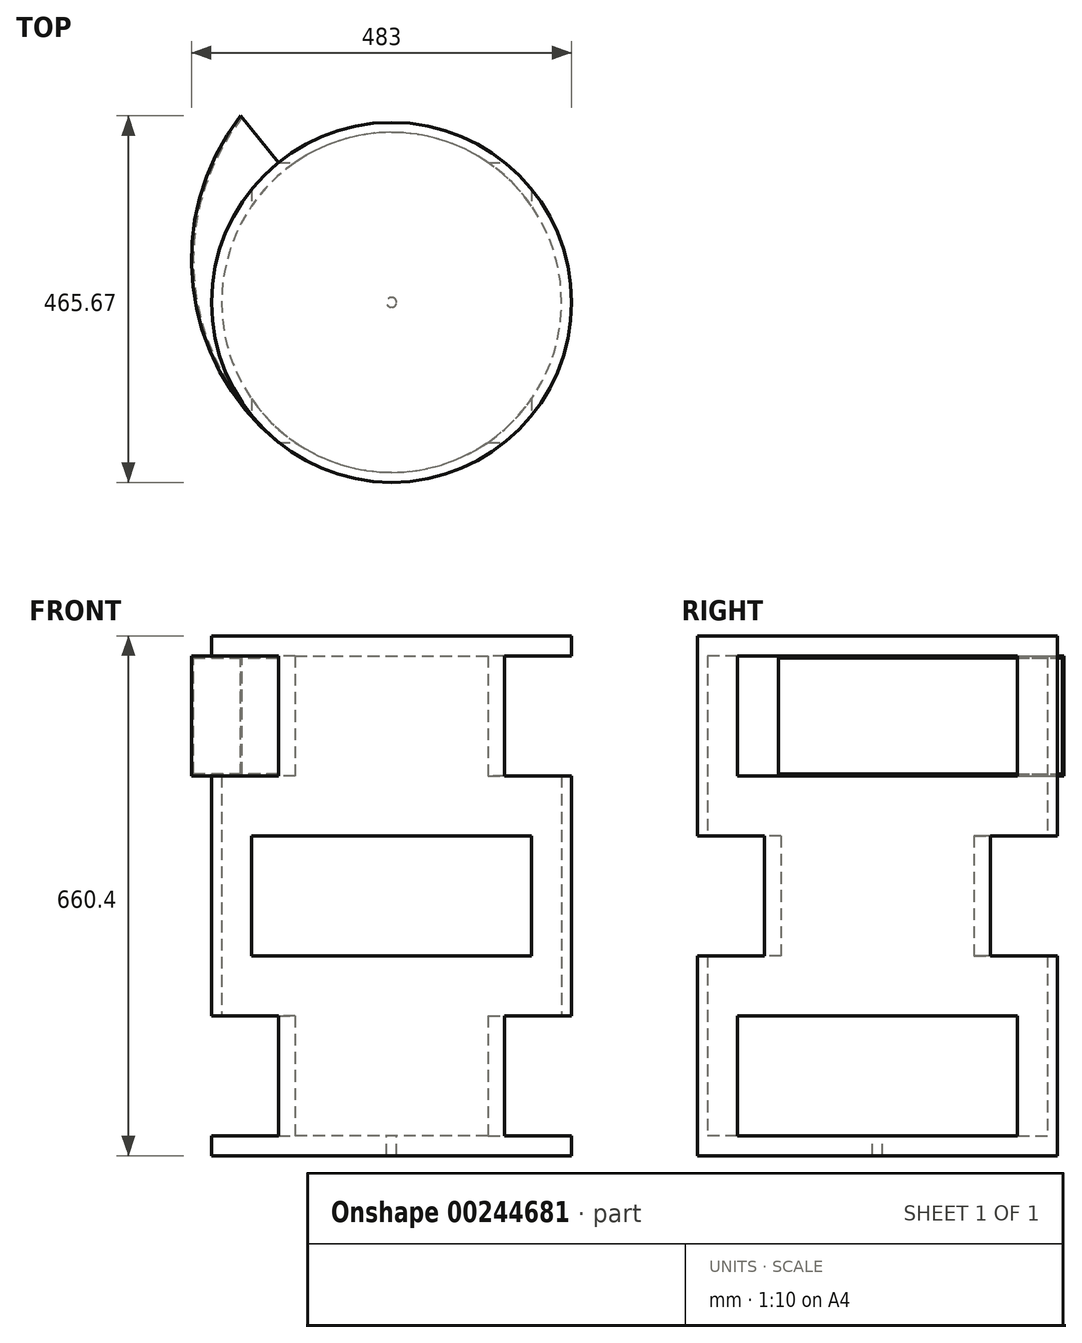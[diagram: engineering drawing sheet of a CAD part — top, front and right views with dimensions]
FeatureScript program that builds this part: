
annotation { "Feature Type Name" : "Feature", "Feature Type Description" : "" }
export const myFeature = defineFeature(function(context is Context, id is Id, definition is map)
    precondition{}
    {
        {
            var Q0;
            Q0=qCreatedBy(makeId("Top.planeOp"),FACE);
            var sketch = newSketch(context, id + "F0", { "sketchPlane" : qUnion([Q0])});
            skCircle(sketch, "E0", {"center": v(0, 0) * mm, "radius": 228.6 * mm});
            skSolve(sketch);
        }
        {
            var Q0;
            Q0=makeQuery(id+"F0.imprint","IMPRINT",FACE,{"disambiguationData":[TD([[makeQuery(id+"F0.imprint","IMPRINT",EDGE,{"derivedFrom":sQuery(id+"F0.wireOp",EDGE,"E0")}),1.0]])]});
            extrude(context, id + "F1", {"entities" : qUnion([Q0]), "depth" : 330.2 * mm, "hasSecondDirection" : true, "secondDirectionOppositeDirection" : true, "secondDirectionDepth" : 330.2 * mm});
        }
        {
            var Q0;
            Q0=makeQuery(id+"F1.opExtrude","CAP_FACE",FACE,{"disambiguationData":[OSD([sQuery(id+"F0.wireOp",EDGE,"E0")])],"isStart":false});
            var Q1;
            Q1=makeQuery(id+"F1.opExtrude","CAP_FACE",FACE,{"disambiguationData":[OSD([sQuery(id+"F0.wireOp",EDGE,"E0")])],"isStart":true});
            shell(context, id + "F2", {"entities" : qUnion([Q0, Q1]), "thickness" : 12.7 * mm});
        }
        {
            var Q0;
            Q0=qCreatedBy(makeId("Front.planeOp"),FACE);
            cPlane(context, id + "F3", {"entities" : qUnion([Q0]), "cplaneType" : CPlaneType.OFFSET, "offset" : 228.6 * mm, "width" : 152.4 * mm, "height" : 152.4 * mm});
        }
        {
            var Q0;
            Q0=qCreatedBy(makeId("Right.planeOp"),FACE);
            cPlane(context, id + "F4", {"entities" : qUnion([Q0]), "cplaneType" : CPlaneType.OFFSET, "offset" : 228.6 * mm, "oppositeDirection" : true, "width" : 152.4 * mm, "height" : 152.4 * mm});
        }
        {
            var Q0;
            Q0=qCreatedBy(makeId("Right.planeOp"),FACE);
            cPlane(context, id + "F5", {"entities" : qUnion([Q0]), "cplaneType" : CPlaneType.OFFSET, "offset" : 228.6 * mm, "width" : 152.4 * mm, "height" : 152.4 * mm});
        }
        {
            var Q0;
            Q0=qCreatedBy(id+"F5.planeOp",FACE);
            var sketch = newSketch(context, id + "F6", { "sketchPlane" : qUnion([Q0])});
            skLineSegment(sketch, "E1", {"start": v(0, 0) * mm, "end": v(0, -304.8) * mm, "construction": true});
            skLineSegment(sketch, "E2", {"start": v(0, 0) * mm, "end": v(0, 330.2) * mm, "construction": true});
            skPoint(sketch, "E3", {"position": v(0, -152.4) * mm});
            skLineSegment(sketch, "E4", {"start": v(0, 0) * mm, "end": v(186.3, 0) * mm, "construction": true});
            skPoint(sketch, "E5.MirrorP", {"position": v(0, 152.4) * mm});
            skLineSegment(sketch, "E6.bottom", {"start": v(177.8, -152.4) * mm, "end": v(-177.8, -152.4) * mm});
            skLineSegment(sketch, "E6.top", {"start": v(177.8, -304.8) * mm, "end": v(-177.8, -304.8) * mm});
            skLineSegment(sketch, "E6.left", {"start": v(177.8, -152.4) * mm, "end": v(177.8, -304.8) * mm});
            skLineSegment(sketch, "E6.right", {"start": v(-177.8, -152.4) * mm, "end": v(-177.8, -304.8) * mm});
            skSolve(sketch);
        }
        {
            var Q0;
            Q0=makeQuery(id+"F6.imprint","IMPRINT",FACE,{"disambiguationData":[TD([[makeQuery(id+"F6.imprint","IMPRINT",EDGE,{"derivedFrom":sQuery(id+"F6.wireOp",EDGE,"E6.bottom")}),1.0]])]});
            extrude(context, id + "F7", {"entities" : qUnion([Q0]), "operationType" : NewBodyOperationType.REMOVE, "oppositeDirection" : true, "depth" : 457.2 * mm});
        }
        {
            var Q0;
            Q0=qCreatedBy(id+"F4.planeOp",FACE);
            var sketch = newSketch(context, id + "F8", { "sketchPlane" : qUnion([Q0])});
            skLineSegment(sketch, "E7", {"start": v(0, 0) * mm, "end": v(0, 304.8) * mm, "construction": true});
            skLineSegment(sketch, "E8", {"start": v(0, 0) * mm, "end": v(-120.1, 0) * mm, "construction": true});
            skPoint(sketch, "E9", {"position": v(0, 152.4) * mm});
            skLineSegment(sketch, "E10.bottom", {"start": v(-177.8, 304.8) * mm, "end": v(177.8, 304.8) * mm});
            skLineSegment(sketch, "E10.top", {"start": v(-177.8, 152.4) * mm, "end": v(177.8, 152.4) * mm});
            skLineSegment(sketch, "E10.left", {"start": v(-177.8, 304.8) * mm, "end": v(-177.8, 152.4) * mm});
            skLineSegment(sketch, "E10.right", {"start": v(177.8, 304.8) * mm, "end": v(177.8, 152.4) * mm});
            skSolve(sketch);
        }
        {
            var Q0;
            Q0=makeQuery(id+"F8.imprint","IMPRINT",FACE,{"disambiguationData":[TD([[makeQuery(id+"F8.imprint","IMPRINT",EDGE,{"derivedFrom":sQuery(id+"F8.wireOp",EDGE,"E10.bottom")}),-1.0]])]});
            extrude(context, id + "F9", {"entities" : qUnion([Q0]), "operationType" : NewBodyOperationType.REMOVE, "depth" : 457.2 * mm});
        }
        {
            var Q0;
            Q0=qCreatedBy(id+"F3.planeOp",FACE);
            var sketch = newSketch(context, id + "F10", { "sketchPlane" : qUnion([Q0])});
            skLineSegment(sketch, "E11", {"start": v(0, 0) * mm, "end": v(0, -330.2) * mm, "construction": true});
            skLineSegment(sketch, "E12.bottom", {"start": v(177.8, -76.2) * mm, "end": v(-177.8, -76.2) * mm});
            skLineSegment(sketch, "E12.top", {"start": v(177.8, 76.2) * mm, "end": v(-177.8, 76.2) * mm});
            skLineSegment(sketch, "E12.left", {"start": v(177.8, -76.2) * mm, "end": v(177.8, 76.2) * mm});
            skLineSegment(sketch, "E12.right", {"start": v(-177.8, -76.2) * mm, "end": v(-177.8, 76.2) * mm});
            skPoint(sketch, "E13", {"position": v(0, -76.2) * mm});
            skSolve(sketch);
        }
        {
            var Q0;
            Q0=makeQuery(id+"F10.imprint","IMPRINT",FACE,{"disambiguationData":[TD([[makeQuery(id+"F10.imprint","IMPRINT",EDGE,{"derivedFrom":sQuery(id+"F10.wireOp",EDGE,"E12.bottom")}),-1.0]])]});
            extrude(context, id + "F11", {"entities" : qUnion([Q0]), "operationType" : NewBodyOperationType.REMOVE, "oppositeDirection" : true, "depth" : 457.2 * mm});
        }
        {
            var Q0;
            Q0=makeQuery(id+"F9.boolean.opBoolean","COPY",FACE,{"disambiguationData":[OD(0.0)],"derivedFrom":makeQuery(id+"F9.opExtrude","SWEPT_FACE",FACE,{"disambiguationData":[OSD([sQuery(id+"F8.wireOp",EDGE,"E10.bottom")])]})});
            var sketch = newSketch(context, id + "F12", { "sketchPlane" : qUnion([Q0])});
            skLineSegment(sketch, "E14", {"start": v(-143.68, -177.8) * mm, "end": v(-143.68, 177.8) * mm, "construction": true});
            skLineSegment(sketch, "E15", {"start": v(-143.68, -177.8) * mm, "end": v(-50.88, -252.8) * mm, "construction": true});
            skLineSegment(sketch, "E16", {"start": v(-143.68, -177.8) * mm, "end": v(-191.58, -237.07) * mm});
            skArc(sketch, "E17", {"start": v(-143.68, 177.8) * mm, "mid": v(-252.44, -19.84) * mm, "end": v(-191.58, -237.07) * mm});
            skArc(sketch, "E18", {"start": v(-143.68, 177.8) * mm, "mid": v(-228.6, 0) * mm, "end": v(-143.68, -177.8) * mm});
            skSolve(sketch);
        }
        {
            var Q0;
            Q0=makeQuery(id+"F12.imprint","IMPRINT",FACE,{"disambiguationData":[TD([[makeQuery(id+"F12.imprint","IMPRINT",EDGE,{"derivedFrom":sQuery(id+"F12.wireOp",EDGE,"E16")}),-1.0]])]});
            extrude(context, id + "F13", {"entities" : qUnion([Q0]), "depth" : 152.4 * mm});
        }
        {
            var Q0;
            Q0=makeQuery(id+"F13.opExtrude","SWEPT_FACE",FACE,{"disambiguationData":[OSD([sQuery(id+"F12.wireOp",EDGE,"E16")])]});
            var Q1;
            Q1=makeQuery(id+"F13.opExtrude","SWEPT_FACE",FACE,{"disambiguationData":[OSD([sQuery(id+"F12.wireOp",EDGE,"E18")])]});
            shell(context, id + "F14", {"entities" : qUnion([Q0, Q1]), "thickness" : 2.54 * mm});
        }
        {
            var Q0;
            Q0=makeQuery(id+"F1.opExtrude","CAP_FACE",FACE,{"disambiguationData":[OSD([sQuery(id+"F0.wireOp",EDGE,"E0")])],"isStart":false});
            var sketch = newSketch(context, id + "F15", { "sketchPlane" : qUnion([Q0])});
            skCircle(sketch, "E19", {"center": v(0, 0) * mm, "radius": 228.6 * mm});
            skSolve(sketch);
        }
        {
            var Q0;
            Q0 = qSketchRegion(id + "F15", true);
            extrude(context, id + "F16", {"entities" : qUnion([Q0]), "operationType" : NewBodyOperationType.ADD, "oppositeDirection" : true, "depth" : 25.4 * mm});
        }
        {
            var Q0;
            Q0=makeQuery(id+"F1.opExtrude","CAP_FACE",FACE,{"disambiguationData":[OSD([sQuery(id+"F0.wireOp",EDGE,"E0")])],"isStart":true});
            var sketch = newSketch(context, id + "F17", { "sketchPlane" : qUnion([Q0])});
            skCircle(sketch, "E20", {"center": v(0, 0) * mm, "radius": 228.6 * mm});
            skSolve(sketch);
        }
        {
            var Q0;
            Q0 = qSketchRegion(id + "F17", true);
            extrude(context, id + "F18", {"entities" : qUnion([Q0]), "operationType" : NewBodyOperationType.ADD, "oppositeDirection" : true, "depth" : 25.4 * mm});
        }
        {
            var Q0;
            Q0=makeQuery(id+"F18.opExtrude","CAP_FACE",FACE,{"disambiguationData":[OSD([sQuery(id+"F17.wireOp",EDGE,"E20")])],"isStart":false});
            var sketch = newSketch(context, id + "F19", { "sketchPlane" : qUnion([Q0])});
            skCircle(sketch, "E21", {"center": v(0, 0) * mm, "radius": 6.35 * mm});
            skSolve(sketch);
        }
        {
            var Q0;
            Q0=makeQuery(id+"F19.imprint","IMPRINT",FACE,{"disambiguationData":[TD([[makeQuery(id+"F19.imprint","IMPRINT",EDGE,{"derivedFrom":sQuery(id+"F19.wireOp",EDGE,"E21")}),1.0]])]});
            extrude(context, id + "F20", {"entities" : qUnion([Q0]), "operationType" : NewBodyOperationType.REMOVE, "endBound" : BoundingType.THROUGH_ALL, "oppositeDirection" : true, "depth" : 25.4 * mm});
        }
    });
